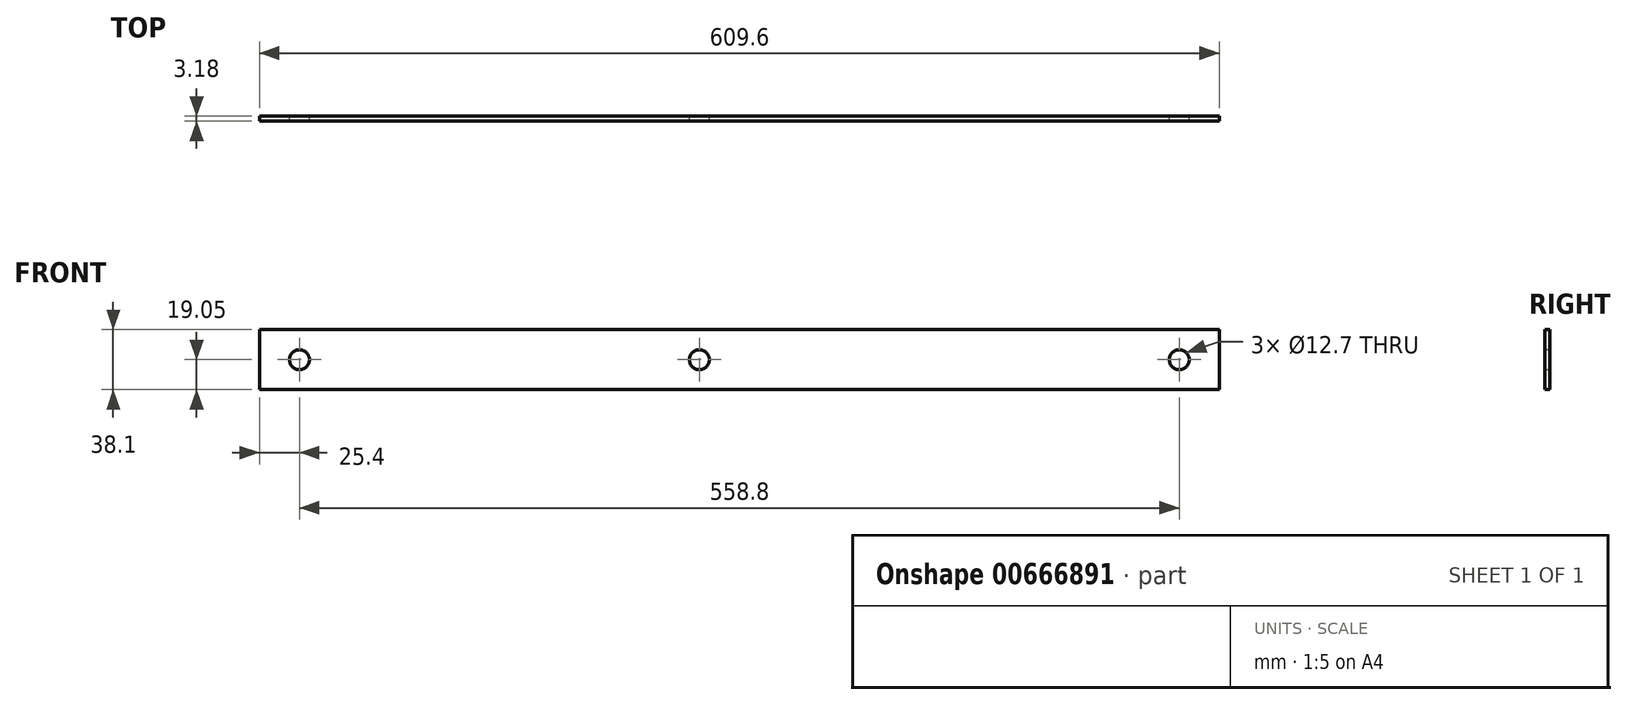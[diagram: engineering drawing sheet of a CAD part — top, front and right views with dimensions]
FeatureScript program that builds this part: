
annotation { "Feature Type Name" : "Feature", "Feature Type Description" : "" }
export const myFeature = defineFeature(function(context is Context, id is Id, definition is map)
    precondition{}
    {
        {
            var Q0;
            Q0=qCreatedBy(makeId("Front.planeOp"),FACE);
            var sketch = newSketch(context, id + "F0", { "sketchPlane" : qUnion([Q0])});
            skLineSegment(sketch, "E0.bottom", {"start": v(0, 0) * mm, "end": v(-609.6, 0) * mm});
            skLineSegment(sketch, "E0.top", {"start": v(0, 38.1) * mm, "end": v(-609.6, 38.1) * mm});
            skLineSegment(sketch, "E0.left", {"start": v(0, 0) * mm, "end": v(0, 38.1) * mm});
            skLineSegment(sketch, "E0.right", {"start": v(-609.6, 0) * mm, "end": v(-609.6, 38.1) * mm});
            skLineSegment(sketch, "E1", {"start": v(-609.6, 19.05) * mm, "end": v(0, 19.05) * mm, "construction": true});
            skPoint(sketch, "E2", {"position": v(-584.2, 19.05) * mm});
            skPoint(sketch, "E3", {"position": v(-330.2, 19.05) * mm});
            skCircle(sketch, "E4", {"center": v(-584.2, 19.05) * mm, "radius": 6.35 * mm});
            skCircle(sketch, "E5", {"center": v(-330.2, 19.05) * mm, "radius": 6.35 * mm});
            skPoint(sketch, "E6", {"position": v(-25.4, 19.05) * mm});
            skCircle(sketch, "E7", {"center": v(-25.4, 19.05) * mm, "radius": 6.35 * mm});
            skSolve(sketch);
        }
        {
            var Q0;
            Q0=makeQuery(id+"F0.imprint","IMPRINT",FACE,{"disambiguationData":[TD([[makeQuery(id+"F0.imprint","IMPRINT",EDGE,{"derivedFrom":sQuery(id+"F0.wireOp",EDGE,"E0.bottom")}),-1.0]])]});
            extrude(context, id + "F1", {"entities" : qUnion([Q0]), "depth" : 3.17 * mm, "offsetDistance" : 25.4 * mm});
        }
    });
